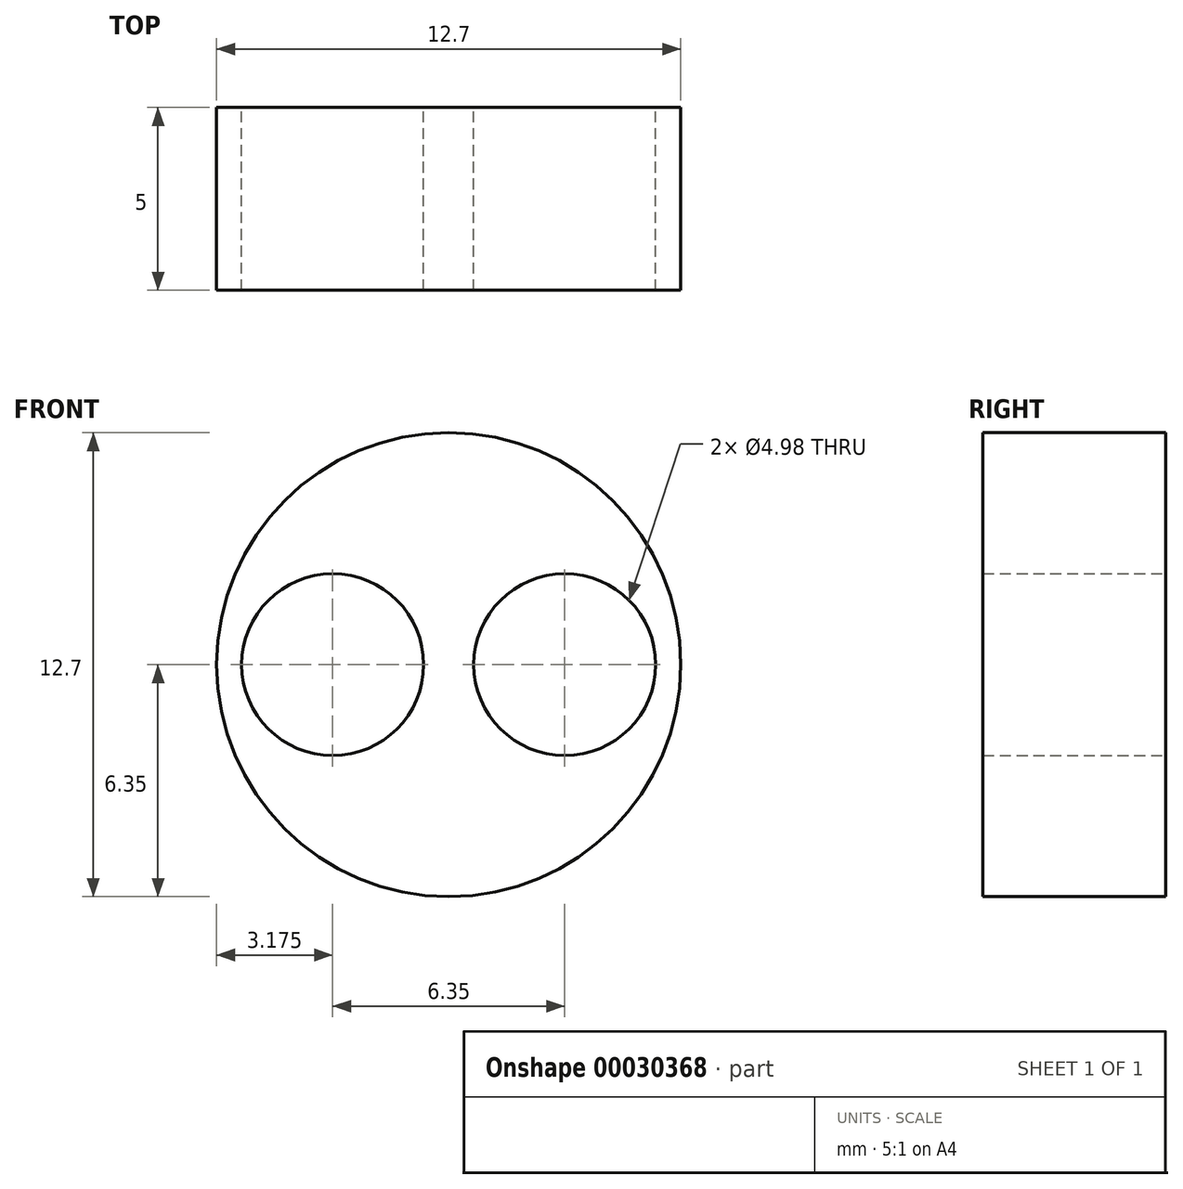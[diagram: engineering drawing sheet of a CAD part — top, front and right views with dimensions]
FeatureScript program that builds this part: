
annotation { "Feature Type Name" : "Feature", "Feature Type Description" : "" }
export const myFeature = defineFeature(function(context is Context, id is Id, definition is map)
    precondition{}
    {
        {
            var Q0;
            Q0=qCreatedBy(makeId("Front.planeOp"),FACE);
            var sketch = newSketch(context, id + "F0", { "sketchPlane" : qUnion([Q0])});
            skCircle(sketch, "E0", {"center": v(0, 0) * mm, "radius": 6.35 * mm});
            skCircle(sketch, "E1", {"center": v(-3.18, 0) * mm, "radius": 2.49 * mm});
            skCircle(sketch, "E2", {"center": v(3.18, 0) * mm, "radius": 2.49 * mm});
            skSolve(sketch);
        }
        {
            var Q0;
            Q0 = qSketchRegion(id + "F0", true);
            extrude(context, id + "F1", {"entities" : qUnion([Q0]), "depth" : 5 * mm});
        }
    });
